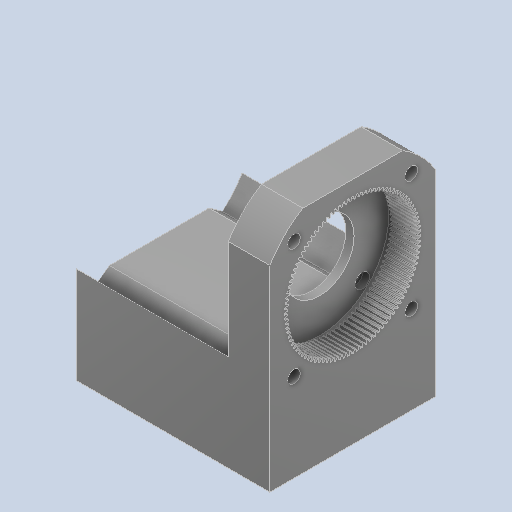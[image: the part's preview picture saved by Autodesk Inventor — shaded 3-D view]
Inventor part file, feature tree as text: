
AUTODESK INVENTOR PART (.ipt)
format: ipt  version: 2022 (Build 260153000, 153)  size: 649,216 bytes
history: mixed  units: in
note: dims shown in document units (in); Inventor stores cm internally (conversion verified against a paired STEP export)
features: extrude x6, sketch x6, plane x1, other x1, imported_body x1
ambient origin geometry x8: Origin, YZ Plane, XZ Plane, XY Plane, X Axis, Y Axis, Z Axis, Center Point
bodies: Solid1 (imported_parasolid)
feature tree (15):
  extrude  "Extrusion1"  Depth=0.3937in TaperAngle=0.0deg
  plane  "Work Plane1"
  extrude  "Extrusion2"  Depth=0.9843in TaperAngle=0.0deg
  extrude  "Extrusion5"  TaperAngle=0.0deg  [1 undecoded]
  extrude  "Extrusion6"  Depth=0.5906in TaperAngle=0.0deg
  extrude  "Extrusion7"  Depth=0.0197in
  extrude  "Extrusion8"  [1 undecoded]
  sketch  "Sketch2"  dims[d1=0.3937in d2=0.0in d3=0.3937in d4=0.0in]
  sketch  "Sketch3"  dims[d9=0.2756in d10=0.9843in d11=0.0in]
  sketch  "Sketch6"  dims[d12=0.7874in d13=0.0in d14=0.0in]
  sketch  "Sketch7"  dims[d15=0.5906in d16=0.0in d17=1.1811in d18=0.0in]
  sketch  "Sketch8"  dims[d7=0.0197in d8=0.0344in]
  sketch  "Sketch9"
  other  "96_Teeth_Gear.STEP"
  imported_body  NMx_Import_Brep_tag  [imported B-rep: ~418 faces, bbox_mm=[70.0, 83.027756, 60.0]]
note: 2 required parameter values undecoded (feature->parameter linkage not recoverable at this tier; creation-order binding heuristic only, values carry confidence <= 0.55)
